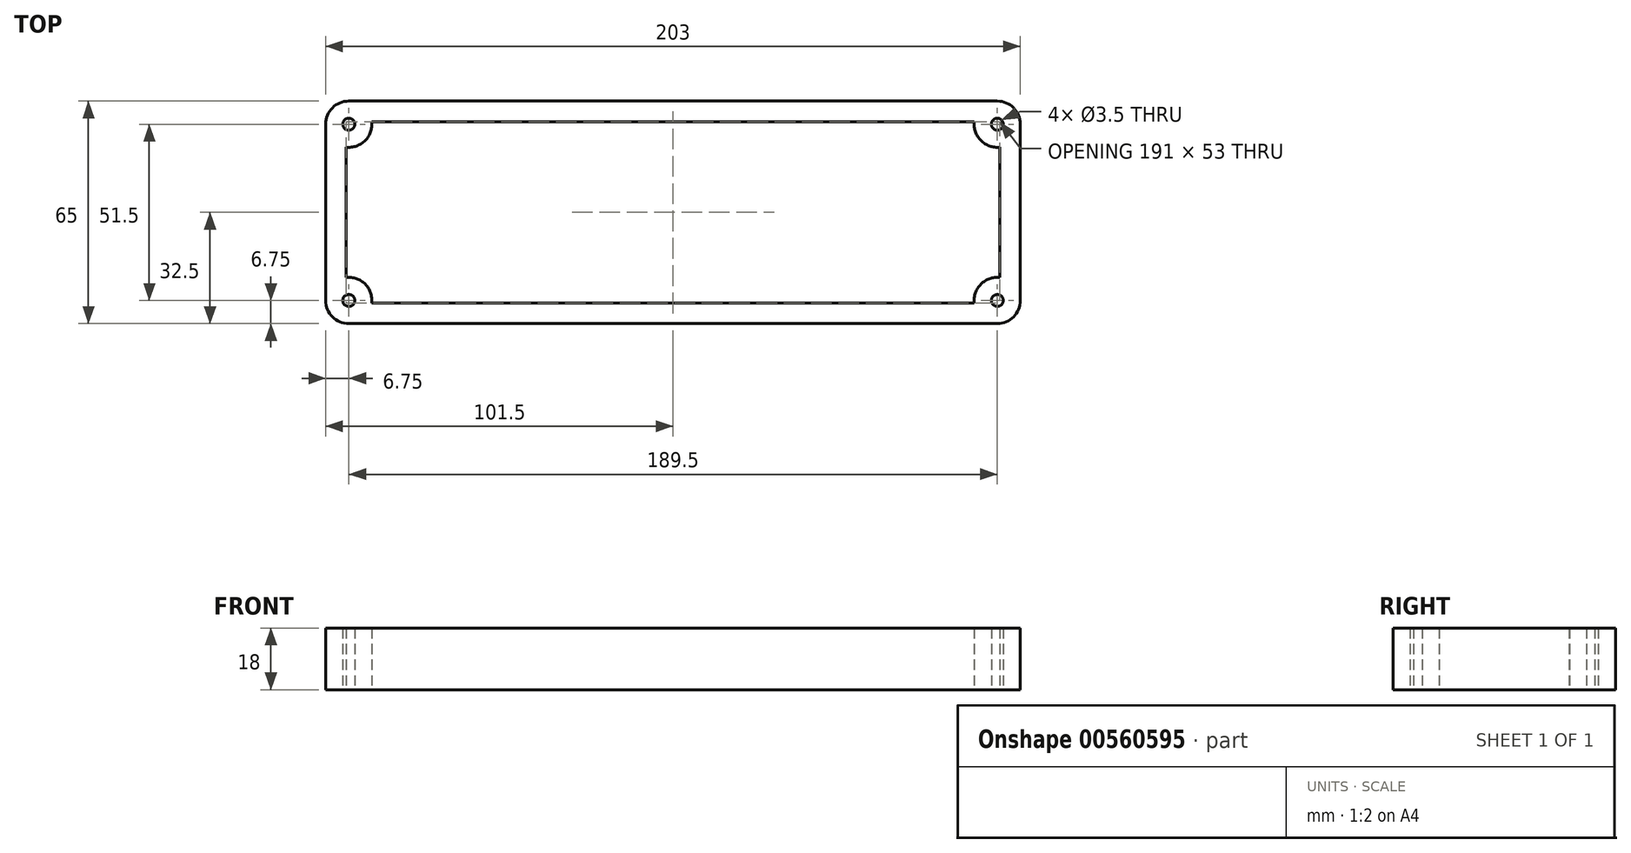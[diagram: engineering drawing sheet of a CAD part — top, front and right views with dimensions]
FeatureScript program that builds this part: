
annotation { "Feature Type Name" : "Feature", "Feature Type Description" : "" }
export const myFeature = defineFeature(function(context is Context, id is Id, definition is map)
    precondition{}
    {
        {
            var Q0;
            Q0=qCreatedBy(makeId("Top.planeOp"),FACE);
            var sketch = newSketch(context, id + "F0", { "sketchPlane" : qUnion([Q0])});
            skLineSegment(sketch, "E0.bottom", {"start": v(94.75, -32.5) * mm, "end": v(-94.75, -32.5) * mm});
            skLineSegment(sketch, "E0.top", {"start": v(94.75, 32.5) * mm, "end": v(-94.75, 32.5) * mm});
            skLineSegment(sketch, "E0.left", {"start": v(101.5, -25.75) * mm, "end": v(101.5, 25.75) * mm});
            skLineSegment(sketch, "E0.right", {"start": v(-101.5, -25.75) * mm, "end": v(-101.5, 25.75) * mm});
            skLineSegment(sketch, "E1.0", {"start": v(88.04, 26.5) * mm, "end": v(6.7, 26.5) * mm});
            skLineSegment(sketch, "E1.2", {"start": v(88.04, -26.5) * mm, "end": v(6.7, -26.5) * mm});
            skLineSegment(sketch, "E1.3", {"start": v(-95.5, -19.04) * mm, "end": v(-95.5, 19.04) * mm});
            skArc(sketch, "E2", {"start": v(-95.5, 19.04) * mm, "mid": v(-89.98, 20.98) * mm, "end": v(-88.04, 26.5) * mm});
            skCircle(sketch, "E3", {"center": v(-94.75, 25.75) * mm, "radius": 1.75 * mm});
            skPoint(sketch, "E4.orphan", {"position": v(-101.5, 32.5) * mm});
            skArc(sketch, "E5.trimOffspring", {"start": v(-94.75, 32.5) * mm, "mid": v(-99.52, 30.52) * mm, "end": v(-101.5, 25.75) * mm});
            skArc(sketch, "E6.MirrorCS", {"start": v(94.75, 32.5) * mm, "mid": v(99.52, 30.52) * mm, "end": v(101.5, 25.75) * mm});
            skCircle(sketch, "E7.MirrorC", {"center": v(94.75, 25.75) * mm, "radius": 1.75 * mm});
            skArc(sketch, "E8.MirrorCS", {"start": v(95.5, 19.04) * mm, "mid": v(89.98, 20.98) * mm, "end": v(88.04, 26.5) * mm});
            skArc(sketch, "E9.MirrorCS", {"start": v(-94.75, -32.5) * mm, "mid": v(-99.52, -30.52) * mm, "end": v(-101.5, -25.75) * mm});
            skCircle(sketch, "E10.MirrorC", {"center": v(-94.75, -25.75) * mm, "radius": 1.75 * mm});
            skArc(sketch, "E11.MirrorCS", {"start": v(-95.5, -19.04) * mm, "mid": v(-89.98, -20.98) * mm, "end": v(-88.04, -26.5) * mm});
            skArc(sketch, "E12.MirrorCS", {"start": v(94.75, -32.5) * mm, "mid": v(99.52, -30.52) * mm, "end": v(101.5, -25.75) * mm});
            skCircle(sketch, "E13.MirrorC", {"center": v(94.75, -25.75) * mm, "radius": 1.75 * mm});
            skArc(sketch, "E14.MirrorCS", {"start": v(95.5, -19.04) * mm, "mid": v(89.98, -20.98) * mm, "end": v(88.04, -26.5) * mm});
            skPoint(sketch, "E15.orphan", {"position": v(-101.5, -32.5) * mm});
            skLineSegment(sketch, "E16.trimOffspring", {"start": v(95.5, -19.04) * mm, "end": v(95.5, 19.04) * mm});
            skPoint(sketch, "E17.orphan", {"position": v(101.5, -32.5) * mm});
            skPoint(sketch, "E18.orphan", {"position": v(101.5, 32.5) * mm});
            skLineSegment(sketch, "E19.trimOffspring", {"start": v(6.7, 26.5) * mm, "end": v(-88.04, 26.5) * mm});
            skLineSegment(sketch, "E20.trimOffspring", {"start": v(6.7, -26.5) * mm, "end": v(-88.04, -26.5) * mm});
            skSolve(sketch);
        }
        {
            var Q0;
            Q0=makeQuery(id+"F0.imprint","IMPRINT",FACE,{"disambiguationData":[TD([[makeQuery(id+"F0.imprint","IMPRINT",EDGE,{"derivedFrom":sQuery(id+"F0.wireOp",EDGE,"E0.bottom")}),-1.0]])]});
            extrude(context, id + "F1", {"entities" : qUnion([Q0]), "depth" : 18 * mm, "offsetDistance" : 25 * mm});
        }
    });
